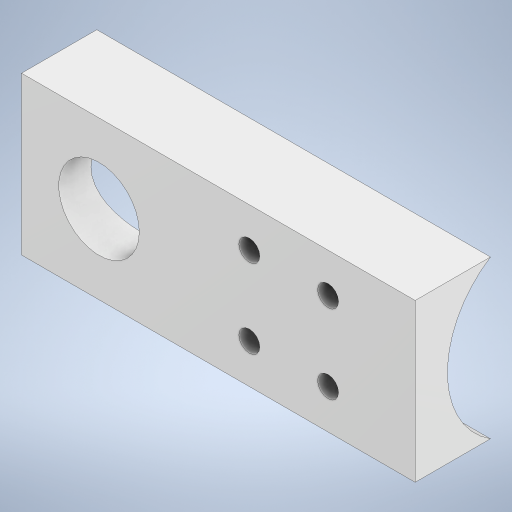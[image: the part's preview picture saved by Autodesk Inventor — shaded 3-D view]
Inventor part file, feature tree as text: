
AUTODESK INVENTOR PART (.ipt)
format: ipt  version: 2023 (Build 270158030, 158C)  size: 259,072 bytes
history: native  units: in
note: dims shown in document units (in); Inventor stores cm internally (conversion verified against a paired STEP export)
features: sketch x4, extrude x3, hole x1, plane x1
ambient origin geometry x8: Origin, YZ Plane, XZ Plane, XY Plane, X Axis, Y Axis, Z Axis, Center Point
bodies: Solid1 (feature_tree)
feature tree (9):
  extrude  "Extrusion1"  Depth=2.0in
  extrude  "Extrusion4"  Depth=1.0236in
  sketch  "Sketch6"  dims[d21=0.0in d22=0.0in]
  hole  "Hole1"  [1 undecoded]
  plane  "Work Plane1"
  extrude  "Extrusion5"  Depth=0.3937in
  sketch  "Sketch1"  dims[d0=2.375in d3=2.0in]
  sketch  "Sketch4"  dims[d4=5.0in d5=0.0in d20=1.0236in]
  sketch  "Sketch7"  dims[d28=0.266in d29=0.2362in d30=0.5906in d31=0.1693in d32=0.5635in d33=0.315in d34=0.8108in d35=1.0in d36=1.0in d38=0.1969in d39=1.0in d40=0.9843in d41=1.0in d42=2.8937in d43=-0.6875in d44=0.4in d45=0.3937in d46=0.0in]
note: 1 required parameter value undecoded (feature->parameter linkage not recoverable at this tier; creation-order binding heuristic only, values carry confidence <= 0.55)
